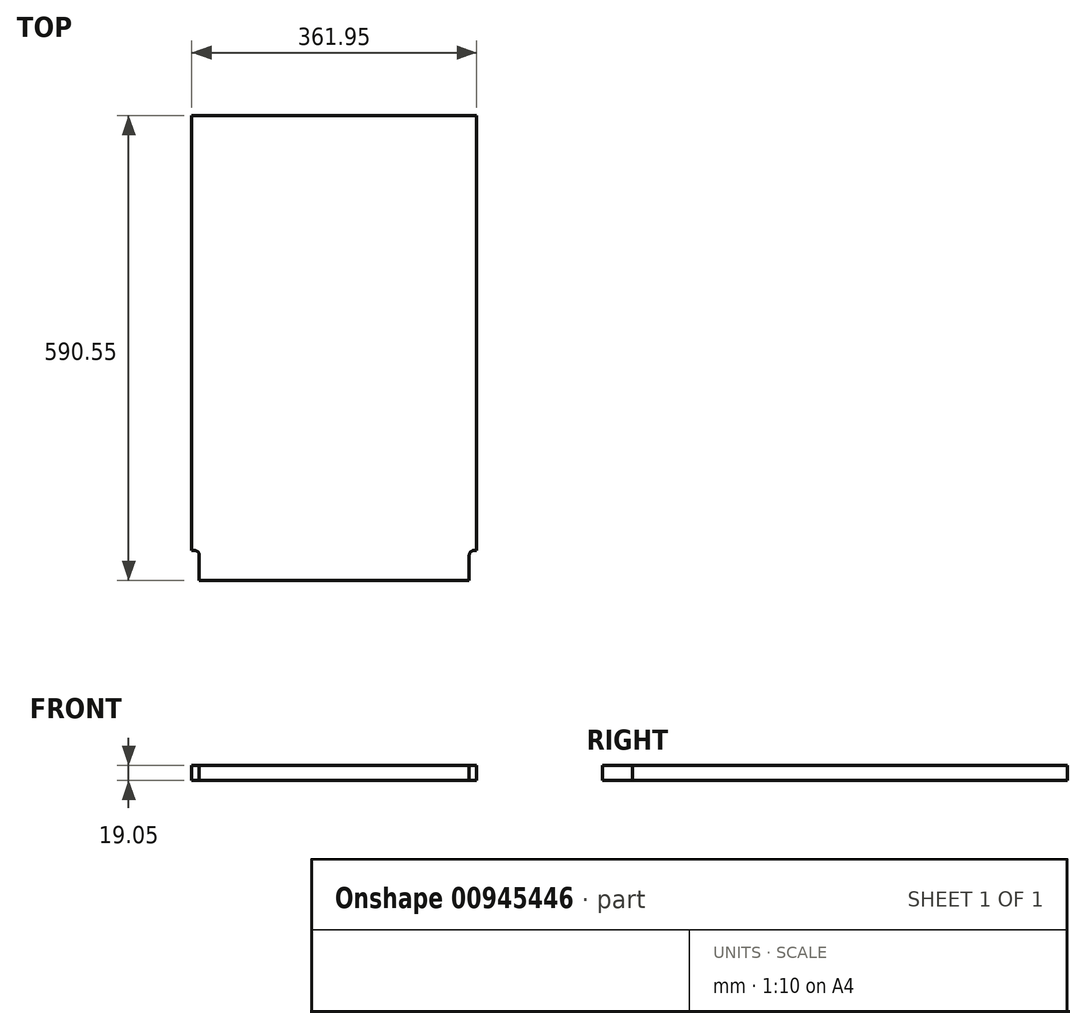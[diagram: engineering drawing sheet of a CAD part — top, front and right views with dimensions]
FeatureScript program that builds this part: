
annotation { "Feature Type Name" : "Feature", "Feature Type Description" : "" }
export const myFeature = defineFeature(function(context is Context, id is Id, definition is map)
    precondition{}
    {
        {
            var Q0;
            Q0=qCreatedBy(makeId("Top.planeOp"),FACE);
            var sketch = newSketch(context, id + "F0", { "sketchPlane" : qUnion([Q0])});
            skLineSegment(sketch, "E0.bottom", {"start": v(0, 0) * mm, "end": v(361.95, 0) * mm});
            skLineSegment(sketch, "E0.top", {"start": v(0, -590.55) * mm, "end": v(361.95, -590.55) * mm});
            skLineSegment(sketch, "E0.left", {"start": v(0, 0) * mm, "end": v(0, -590.55) * mm});
            skLineSegment(sketch, "E0.right", {"start": v(361.95, 0) * mm, "end": v(361.95, -590.55) * mm});
            skLineSegment(sketch, "E1", {"start": v(9.53, -590.55) * mm, "end": v(9.53, -558.8) * mm});
            skLineSegment(sketch, "E2", {"start": v(0, -552.45) * mm, "end": v(3.18, -552.45) * mm});
            skArc(sketch, "E3", {"start": v(9.53, -558.8) * mm, "mid": v(7.67, -554.3) * mm, "end": v(3.18, -552.45) * mm});
            skLineSegment(sketch, "E4", {"start": v(180.97, 0) * mm, "end": v(180.98, -590.55) * mm, "construction": true});
            skLineSegment(sketch, "E5.MirrorCS", {"start": v(361.95, -552.45) * mm, "end": v(358.78, -552.45) * mm});
            skArc(sketch, "E6.MirrorCS", {"start": v(352.43, -558.8) * mm, "mid": v(354.28, -554.3) * mm, "end": v(358.78, -552.45) * mm});
            skLineSegment(sketch, "E7.MirrorCS", {"start": v(352.43, -590.55) * mm, "end": v(352.43, -558.8) * mm});
            skSolve(sketch);
        }
        {
            var Q0;
            {var subQ1=sQuery(id+"F0.wireOp",EDGE,"E0.bottom");Q0=makeQuery(id+"F0.imprint","IMPRINT",FACE,{"disambiguationData":[TD([[makeQuery(id+"F0.imprint","IMPRINT",EDGE,{"derivedFrom":subQ1}),-1.0]])]});}
            extrude(context, id + "F1", {"entities" : qUnion([Q0]), "depth" : 19.05 * mm, "offsetDistance" : 25.4 * mm});
        }
    });
